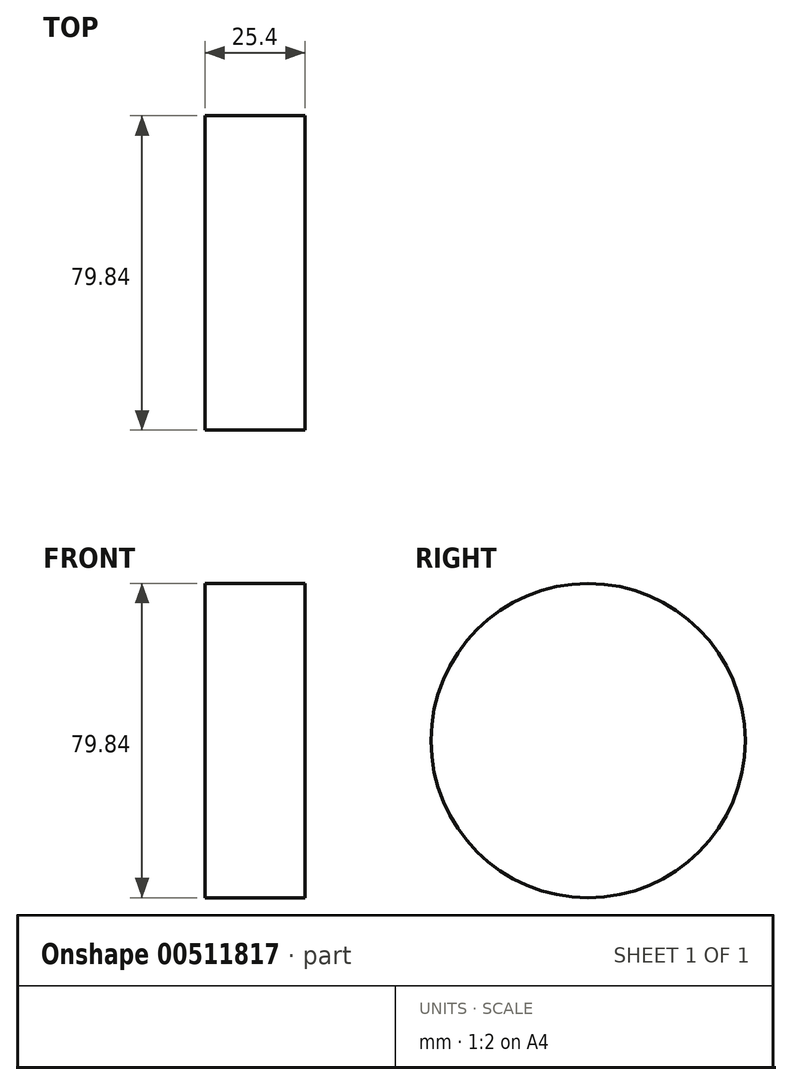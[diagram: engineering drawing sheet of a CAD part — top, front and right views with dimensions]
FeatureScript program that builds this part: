
annotation { "Feature Type Name" : "Feature", "Feature Type Description" : "" }
export const myFeature = defineFeature(function(context is Context, id is Id, definition is map)
    precondition{}
    {
        {
            var Q0;
            Q0=qCreatedBy(makeId("Right.planeOp"),FACE);
            var sketch = newSketch(context, id + "F0", { "sketchPlane" : qUnion([Q0])});
            skCircle(sketch, "E0", {"center": v(0, 0) * mm, "radius": 39.92 * mm});
            skSolve(sketch);
        }
        {
            var Q0;
            Q0 = qSketchRegion(id + "F0", true);
            extrude(context, id + "F1", {"entities" : qUnion([Q0]), "depth" : 25.4 * mm});
        }
    });
